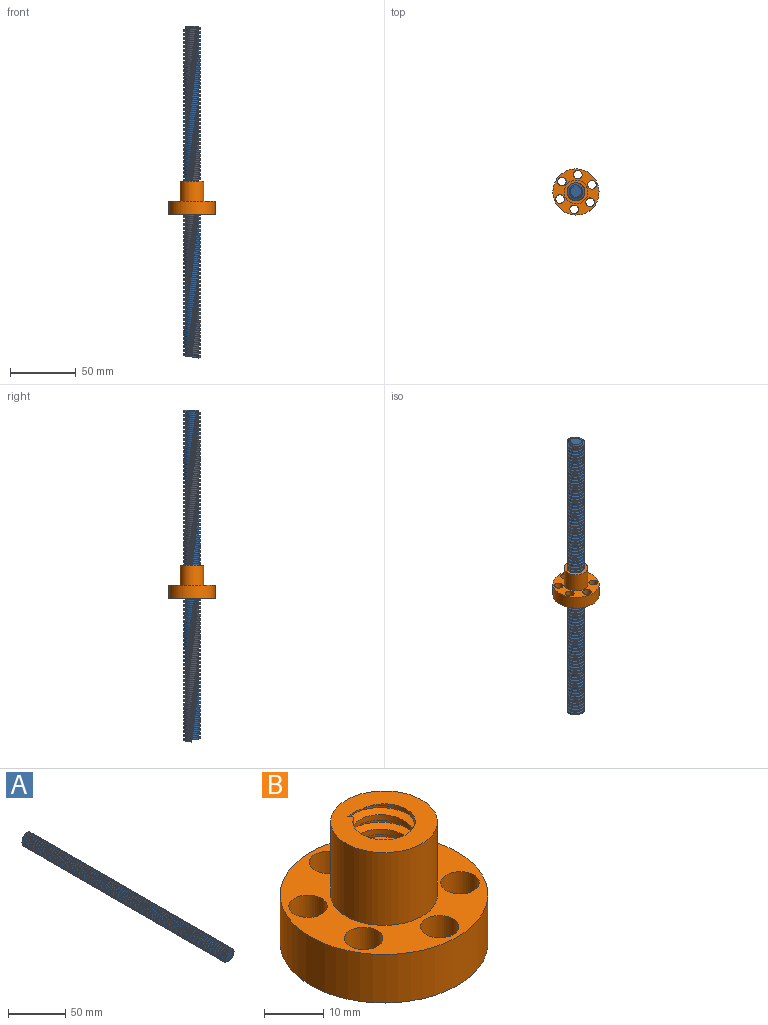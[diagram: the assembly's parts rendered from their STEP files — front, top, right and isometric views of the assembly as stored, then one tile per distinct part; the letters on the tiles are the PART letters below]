
ASSEMBLY  parts=2 mates=1
PART A: 11 faces, bbox 13.7x252.8x15.8 mm
  f0: cylinder r=5.25mm len=249mm, axis (0,1,0), area -2181.5mm2, adj f1,f4,f5,f6,f8,f10
  f1: plane 10.5x10.5mm, normal (0,-1,0), area 86.6mm2, adj f0,f3
  f2: plane 9.67x8.67mm, normal (0,1,0), area 60.4mm2, adj f5,f7,f8,f10
  f3: cylinder r=5.25mm len=10.5mm, axis (0,1,0), area 14.8mm2, adj f1,f4,f6
  f4: plane 1.89x1.5mm, normal (0,0,-1), area 2.2mm2, adj f0,f3,f6,f8,f9
  f5: plane 2.17x1.89mm, normal (0.87,0,-0.5), area 2.7mm2, adj f0,f2,f6,f7,f8,f9,f10
  f6: bspline ~250.89x15.59mm, area 4895.2mm2, adj f0,f3,f4,f5,f9
  f7: cylinder r=5.25mm len=2.63mm, axis (0,1,0), area 0.3mm2, adj f2,f5,f8
  f8: bspline ~251.15x15.59mm, area 4899.6mm2, adj f0,f2,f4,f5,f7,f9,f10
  f9: cylinder r=6.75mm len=251.11mm, axis (0,1,0), area 3930.4mm2, adj f4,f5,f6,f8
  f10: cone r=5.25mm half-angle=45deg, axis (0,-1,0), area 29.6mm2, adj f0,f2,f5,f8
PART B: 17 faces, bbox 35.1x35.1x26 mm
  f0: plane 18.08x18.08mm, normal (0,0,1), area 166.4mm2, adj f9,f11,f15,f16
  f1: cylinder r=3.25mm len=10mm, axis (0,0,1), area 204.2mm2, adj f7,f8
  f2: cylinder r=3.25mm len=10mm, axis (0,0,1), area 204.2mm2, adj f7,f8
  f3: cylinder r=3.25mm len=10mm, axis (0,0,1), area 204.2mm2, adj f7,f8
  f4: cylinder r=3.25mm len=10mm, axis (0,0,1), area 204.2mm2, adj f7,f8
  f5: cylinder r=3.25mm len=10mm, axis (0,0,1), area 204.2mm2, adj f7,f8
  f6: cylinder r=17.5mm len=35mm, axis (0,0,-1), area 1099.6mm2, adj f7,f8
  f7: plane 35x35mm, normal (0,0,1), area 508.5mm2, adj f1,f2,f3,f4,f5,f6,f9,f10
  f8: plane 35.07x35.07mm, normal (0,0,-1), area 649.9mm2, adj f1,f2,f3,f4,f5,f6,f10,f11
  f9: cylinder r=9mm len=18mm, axis (0,0,-1), area 848.2mm2, adj f0,f7
  f10: cylinder r=3.25mm len=10mm, axis (0,0,1), area 204.2mm2, adj f7,f8
  f11: cylinder r=5.25mm len=25mm, axis (0,0,1), area 253.1mm2, adj f0,f8,f12,f14,f15,f16
  f12: plane 0.97x0.25mm, normal (0,1,0), area 0.1mm2, adj f8,f11,f15
  f13: cylinder r=6.75mm len=24.86mm, axis (0,0,-1), area 280.1mm2, adj f8,f14,f15,f16
  f14: bspline ~24.39x15.59mm, area 462.4mm2, adj f8,f11,f13,f16
  f15: bspline ~25.89x15.59mm, area 485.5mm2, adj f0,f8,f11,f12,f13,f16
  f16: plane 1.64x1.3mm, normal (0.87,0.5,0), area 2.1mm2, adj f0,f11,f13,f14,f15
PLACE A rot(axis=(0,0.71,0.71),180deg) t=(0,0,-125)mm fixed
PLACE B rot(axis=(0,0,-1),6.1deg) t=(0,0,-142.58)mm
MATE cylindrical B.f9 <-> A.f0  axis (0,0,-1) through (0,0,-125.08)mm
